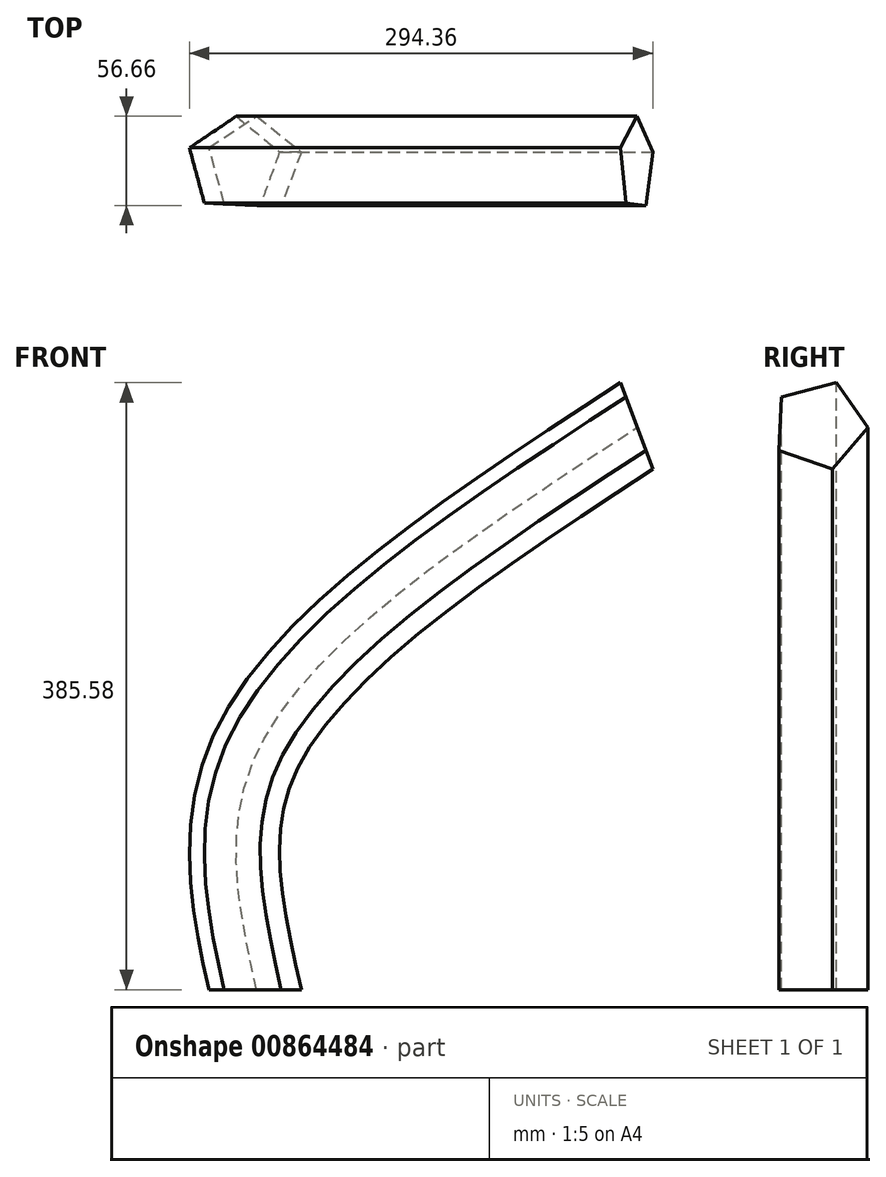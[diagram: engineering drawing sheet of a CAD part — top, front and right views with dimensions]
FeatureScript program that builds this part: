
annotation { "Feature Type Name" : "Feature", "Feature Type Description" : "" }
export const myFeature = defineFeature(function(context is Context, id is Id, definition is map)
    precondition{}
    {
        {
            var Q0;
            Q0=qCreatedBy(makeId("Top.planeOp"),FACE);
            var sketch = newSketch(context, id + "F0", { "sketchPlane" : qUnion([Q0])});
            skCircle(sketch, "E0.cCircle", {"center": v(0, 0) * mm, "radius": 25 * mm, "construction": true});
            skLineSegment(sketch, "E0.0", {"start": v(29.79, 8.22) * mm, "end": v(17.02, -25.8) * mm});
            skLineSegment(sketch, "E0.1", {"start": v(17.02, -25.8) * mm, "end": v(-19.27, -24.16) * mm});
            skLineSegment(sketch, "E0.2", {"start": v(-19.27, -24.16) * mm, "end": v(-28.93, 10.86) * mm});
            skLineSegment(sketch, "E0.3", {"start": v(-28.93, 10.86) * mm, "end": v(1.4, 30.87) * mm});
            skLineSegment(sketch, "E0.4", {"start": v(1.4, 30.87) * mm, "end": v(29.79, 8.22) * mm});
            skPoint(sketch, "E0.0.midPoint", {"position": v(23.4, -8.79) * mm});
            skSolve(sketch);
        }
        {
            var Q0;
            Q0=qCreatedBy(makeId("Front.planeOp"),FACE);
            var sketch = newSketch(context, id + "F1", { "sketchPlane" : qUnion([Q0])});
            skFitSpline(sketch, "E1", {"points": [v(0, 0) * mm, v(0, 150.18) * mm, v(242.58, 358.5) * mm], "startDerivative": vector(-83.12, 373.02) * mm, "endDerivative": vector(530.11, 345.67) * mm});
            skSolve(sketch);
        }
        {
            var Q0;
            Q0=makeQuery(id+"F0.imprint","IMPRINT",FACE,{"disambiguationData":[TD([[makeQuery(id+"F0.imprint","IMPRINT",EDGE,{"derivedFrom":sQuery(id+"F0.wireOp",EDGE,"E0.0")}),-1.0]])]});
            var Q1;
            Q1=sQuery(id+"F1.wireOp",EDGE,"E1");
            sweep(context, id + "F2", {"profiles" : qUnion([Q0]), "path" : qUnion([Q1])});
        }
    });
